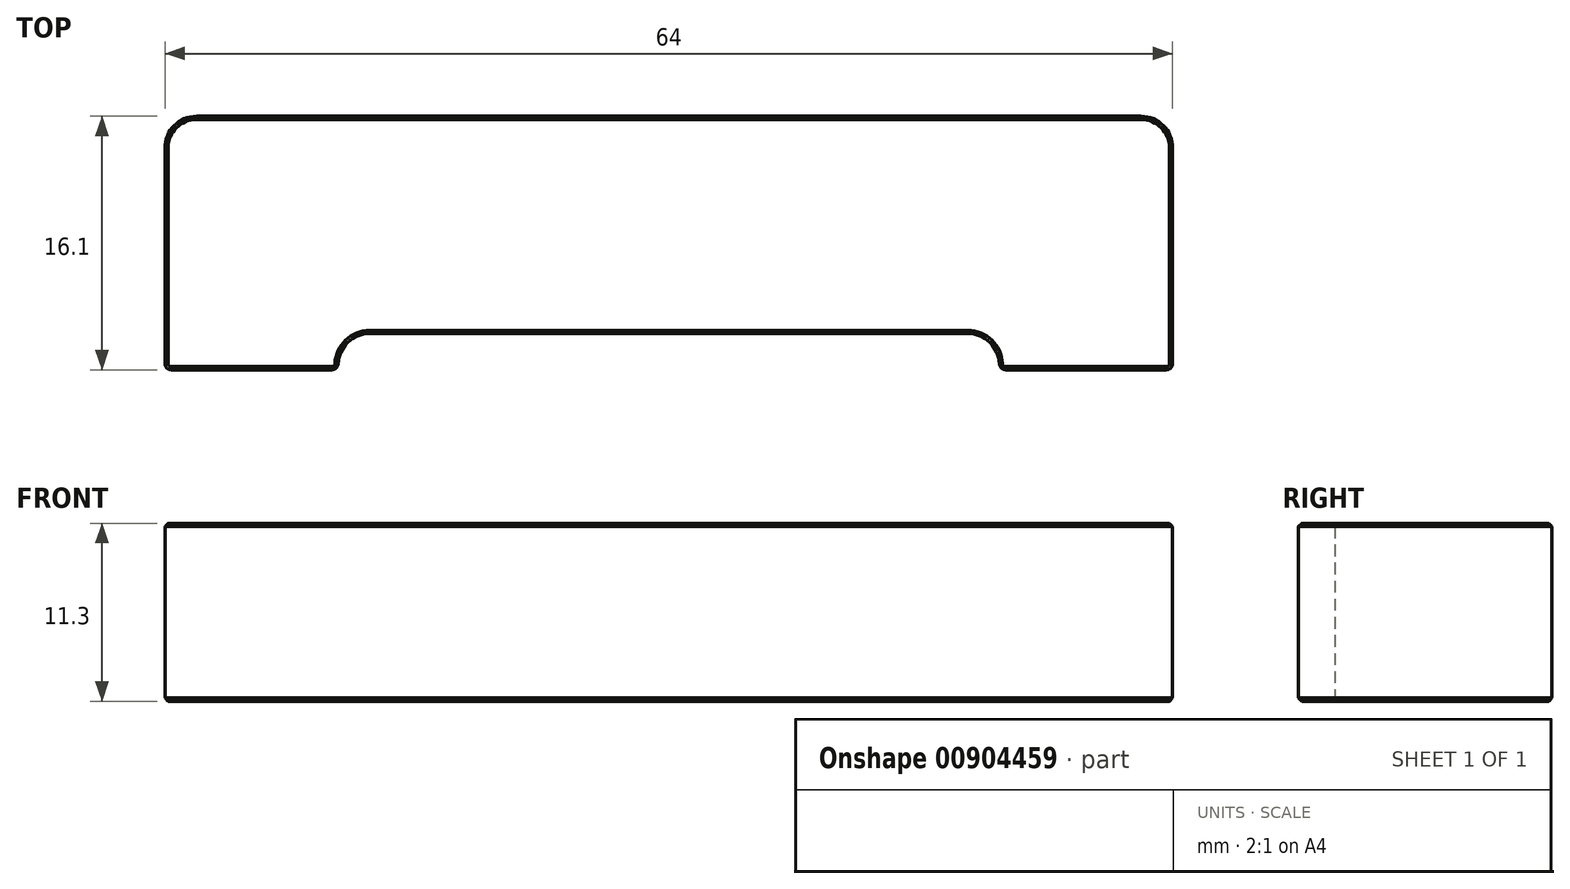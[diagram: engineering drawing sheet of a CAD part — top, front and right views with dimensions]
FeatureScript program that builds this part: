
annotation { "Feature Type Name" : "Feature", "Feature Type Description" : "" }
export const myFeature = defineFeature(function(context is Context, id is Id, definition is map)
    precondition{}
    {
        {
            var Q0;
            Q0=qCreatedBy(makeId("Top.planeOp"),FACE);
            var sketch = newSketch(context, id + "F0", { "sketchPlane" : qUnion([Q0])});
            skLineSegment(sketch, "E0.bottom", {"start": v(-32, -8.05) * mm, "end": v(-21, -8.05) * mm});
            skLineSegment(sketch, "E0.top", {"start": v(-30, 8.05) * mm, "end": v(30, 8.05) * mm});
            skLineSegment(sketch, "E0.left", {"start": v(-32, -8.05) * mm, "end": v(-32, 6.05) * mm});
            skLineSegment(sketch, "E0.right", {"start": v(32, -8.05) * mm, "end": v(32, 6.05) * mm});
            skPoint(sketch, "E0.middle", {"position": v(0, 0) * mm});
            skLineSegment(sketch, "E1", {"start": v(-19, -5.75) * mm, "end": v(19, -5.75) * mm});
            skLineSegment(sketch, "E2", {"start": v(-21, -7.75) * mm, "end": v(-21, -8.05) * mm});
            skLineSegment(sketch, "E3", {"start": v(21, -7.75) * mm, "end": v(21, -8.05) * mm});
            skLineSegment(sketch, "E4.trimOffspring", {"start": v(21, -8.05) * mm, "end": v(32, -8.05) * mm});
            skPoint(sketch, "E5.orphan", {"position": v(-32, -5.75) * mm});
            skPoint(sketch, "E6.visualSharp", {"position": v(-32, 8.05) * mm});
            skArc(sketch, "E6.filletArc", {"start": v(-30, 8.05) * mm, "mid": v(-31.41, 7.46) * mm, "end": v(-32, 6.05) * mm});
            skPoint(sketch, "E7.visualSharp", {"position": v(32, 8.05) * mm});
            skArc(sketch, "E7.filletArc", {"start": v(32, 6.05) * mm, "mid": v(31.41, 7.46) * mm, "end": v(30, 8.05) * mm});
            skPoint(sketch, "E8.visualSharp", {"position": v(-21, -5.75) * mm});
            skArc(sketch, "E8.filletArc", {"start": v(-19, -5.75) * mm, "mid": v(-20.41, -6.34) * mm, "end": v(-21, -7.75) * mm});
            skPoint(sketch, "E9.visualSharp", {"position": v(21, -5.75) * mm});
            skArc(sketch, "E9.filletArc", {"start": v(21, -7.75) * mm, "mid": v(20.41, -6.34) * mm, "end": v(19, -5.75) * mm});
            skSolve(sketch);
        }
        {
            var Q0;
            Q0=makeQuery(id+"F0.imprint","IMPRINT",FACE,{"disambiguationData":[TD([[makeQuery(id+"F0.imprint","IMPRINT",EDGE,{"derivedFrom":sQuery(id+"F0.wireOp",EDGE,"E0.bottom")}),1.0]])]});
            extrude(context, id + "F1", {"entities" : qUnion([Q0]), "depth" : 11.3 * mm, "offsetDistance" : 25 * mm});
        }
        {
            var Q0;
            Q0=makeQuery(id+"F1.opExtrude","SWEPT_EDGE",EDGE,{"disambiguationData":[OSD([sQuery(id+"F0.wireOp",EDGE,"E0.bottom"),sQuery(id+"F0.wireOp",EDGE,"E0.left")])]});
            var Q1;
            Q1=makeQuery(id+"F1.opExtrude","SWEPT_EDGE",EDGE,{"disambiguationData":[OSD([sQuery(id+"F0.wireOp",EDGE,"E0.bottom"),sQuery(id+"F0.wireOp",EDGE,"E2")])]});
            var Q2;
            Q2=makeQuery(id+"F1.opExtrude","SWEPT_EDGE",EDGE,{"disambiguationData":[OSD([sQuery(id+"F0.wireOp",EDGE,"E3"),sQuery(id+"F0.wireOp",EDGE,"E4.trimOffspring")])]});
            var Q3;
            Q3=makeQuery(id+"F1.opExtrude","SWEPT_EDGE",EDGE,{"disambiguationData":[OSD([sQuery(id+"F0.wireOp",EDGE,"E0.right"),sQuery(id+"F0.wireOp",EDGE,"E4.trimOffspring")])]});
            fillet(context, id + "F2", {"entities" : qUnion([Q0, Q1, Q2, Q3]), "radius" : 0.4 * mm, "tangentPropagation" : true, "allowEdgeOverflow" : false});
        }
        {
            var Q0;
            Q0=makeQuery(id+"F1.opExtrude","CAP_FACE",FACE,{"disambiguationData":[OSD([sQuery(id+"F0.wireOp",EDGE,"E0.bottom"),sQuery(id+"F0.wireOp",EDGE,"E0.top"),sQuery(id+"F0.wireOp",EDGE,"E0.left"),sQuery(id+"F0.wireOp",EDGE,"E0.right"),sQuery(id+"F0.wireOp",EDGE,"E1"),sQuery(id+"F0.wireOp",EDGE,"E2"),sQuery(id+"F0.wireOp",EDGE,"E3"),sQuery(id+"F0.wireOp",EDGE,"E4.trimOffspring"),sQuery(id+"F0.wireOp",EDGE,"E6.filletArc"),sQuery(id+"F0.wireOp",EDGE,"E7.filletArc"),sQuery(id+"F0.wireOp",EDGE,"E8.filletArc"),sQuery(id+"F0.wireOp",EDGE,"E9.filletArc")])],"isStart":true});
            var Q1;
            Q1=makeQuery(id+"F1.opExtrude","CAP_FACE",FACE,{"disambiguationData":[OSD([sQuery(id+"F0.wireOp",EDGE,"E0.bottom"),sQuery(id+"F0.wireOp",EDGE,"E0.top"),sQuery(id+"F0.wireOp",EDGE,"E0.left"),sQuery(id+"F0.wireOp",EDGE,"E0.right"),sQuery(id+"F0.wireOp",EDGE,"E1"),sQuery(id+"F0.wireOp",EDGE,"E2"),sQuery(id+"F0.wireOp",EDGE,"E3"),sQuery(id+"F0.wireOp",EDGE,"E4.trimOffspring"),sQuery(id+"F0.wireOp",EDGE,"E6.filletArc"),sQuery(id+"F0.wireOp",EDGE,"E7.filletArc"),sQuery(id+"F0.wireOp",EDGE,"E8.filletArc"),sQuery(id+"F0.wireOp",EDGE,"E9.filletArc")])],"isStart":false});
            chamfer(context, id + "F3", {"entities" : qUnion([Q0, Q1]), "width" : 0.2 * mm, "tangentPropagation" : true});
        }
    });
